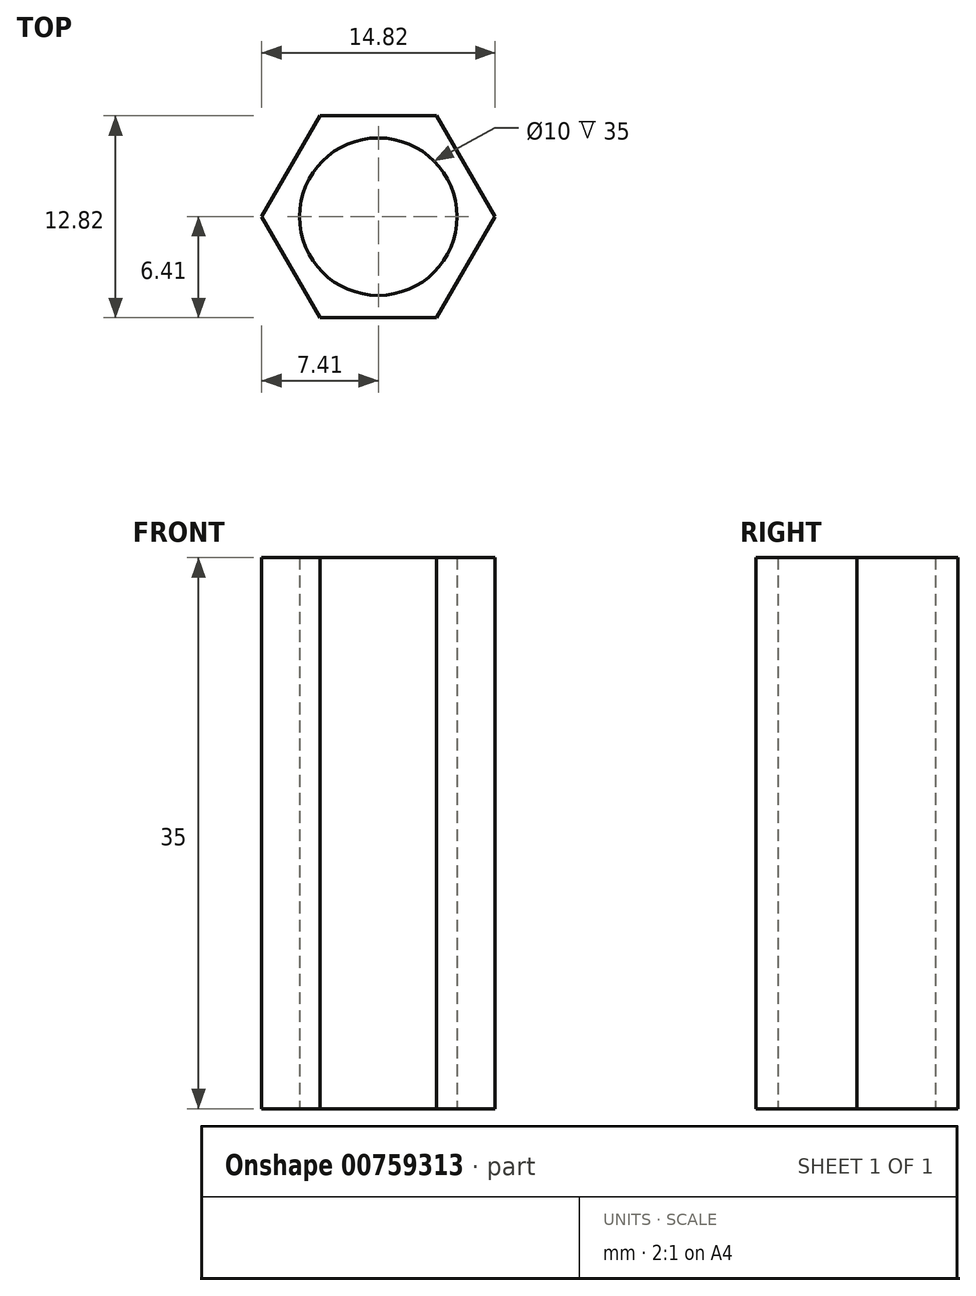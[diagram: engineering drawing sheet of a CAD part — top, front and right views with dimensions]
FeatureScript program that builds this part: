
annotation { "Feature Type Name" : "Feature", "Feature Type Description" : "" }
export const myFeature = defineFeature(function(context is Context, id is Id, definition is map)
    precondition{}
    {
        {
            var Q0;
            Q0=qCreatedBy(makeId("Top.planeOp"),FACE);
            var sketch = newSketch(context, id + "F0", { "sketchPlane" : qUnion([Q0])});
            skCircle(sketch, "E0.cCircle", {"center": v(0, 0) * mm, "radius": 6.41 * mm, "construction": true});
            skLineSegment(sketch, "E0.0", {"start": v(-3.7, 6.41) * mm, "end": v(3.7, 6.41) * mm});
            skLineSegment(sketch, "E0.1", {"start": v(3.7, 6.41) * mm, "end": v(7.4, 0) * mm});
            skLineSegment(sketch, "E0.2", {"start": v(7.4, 0) * mm, "end": v(3.7, -6.41) * mm});
            skLineSegment(sketch, "E0.3", {"start": v(3.7, -6.41) * mm, "end": v(-3.7, -6.41) * mm});
            skLineSegment(sketch, "E0.4", {"start": v(-3.7, -6.41) * mm, "end": v(-7.4, 0) * mm});
            skLineSegment(sketch, "E0.5", {"start": v(-7.4, 0) * mm, "end": v(-3.7, 6.41) * mm});
            skPoint(sketch, "E0.0.midPoint", {"position": v(0, 6.41) * mm});
            skCircle(sketch, "E1", {"center": v(0, 0) * mm, "radius": 5 * mm});
            skSolve(sketch);
        }
        {
            var Q0;
            Q0=makeQuery(id+"F0.imprint","IMPRINT",FACE,{"disambiguationData":[TD([[makeQuery(id+"F0.imprint","IMPRINT",EDGE,{"derivedFrom":sQuery(id+"F0.wireOp",EDGE,"E0.0")}),-1.0]])]});
            extrude(context, id + "F1", {"entities" : qUnion([Q0]), "depth" : 35 * mm, "offsetDistance" : 25 * mm});
        }
    });
